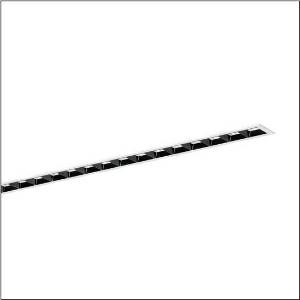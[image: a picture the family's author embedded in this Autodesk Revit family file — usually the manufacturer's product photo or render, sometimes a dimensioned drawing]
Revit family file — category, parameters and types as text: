
# Revit family: silica_r__21_51mx14dp4awb_d613
name_source: partatom
category: Lighting Fixtures
units: mm (PartAtom-declared; Revit-internal decimal feet)

## family parameters
Cut with Voids When Loaded = No
Host = Face
Light Source = No
Part Type = Normal
Room Calculation Point = No
Round Connector Dimension = Use Diameter
Shared = No

## types (1)
- --- (1 x LED, 11880 lm, 80.7 W, 4000K)
    Apparent Load = 81 VA
    CIE Flux Codes = 74 94 99 100 100
    Color Rendering = 80
    Color Temperature = 4000K
    Default Elevation = 1800 mm
    Description = Silica® 21, office luminaire, primary light control with darklight reflector, of PMMA, black, light emission: direct distribution, primary light characteristic: asymmetric, installation type: recessed, LED, rated luminous flux: 11.880lm, luminous efficacy: 147lm/W, light colour: 840, colour temperature: 4000K, control gear: DALI 2, with terminal, 3+2-pole, max. 2.5mm², mains connection: 220..240V, AC, 50/60Hz, rated input power: 80.7W, luminaire housing, of aluminium, traffic white (RAL 9016), length: 3.300mm, width: 79mm, height: 53mm, protection rating (complete): IP20, insulation class (complete): insulation class I (protective earthing), certification: CE, ENEC, VDE, permissible operating ambient temperature: 0..+35°C, standard: EN 50419, packaging unit: 1 piece
    Height = 0 mm  [stored 0 ft]
    Lamp = 1 x LED
    Lamp Light Flux = 11880 lm
    Lamp Power = 80.7 W
    Lamp count = 1
    Length = 3327 mm
    Luminous efficacy = 147 lm/W
    Manufacturer = Siteco
    ModVariant = No
    Model = 51MX14DP4AWB
    Mounting Place = Ceiling
    Mounting Type = Recessed
    Number of Poles = 1
    OnlyDefault = Yes
    Power Factor = 1
    Product Name = Silica® 21
    Product group = office luminaire | ceiling recessed
    ProductGroupID = 400
    Protection Class = Protection class I
    Protection Degree = IP 20
    RLX_Detail_Level = 1
    RLX_Emergency_Light_Flux = 0 lm
    RLX_Emergency_Type = 0
    RLX_Emergency_Type_DB = No
    RlxData = <blob elided: 33281 chars, md5=3f512f17>
    Socket = socket
    Standby Power = 0 W
    System Light Flux = 11880 lm
    System Power = 81 W
    Type Comments = factory setting: luminous flux: 100 % | dim-lin: 254 | 418 mA
    Type Image = l_1335880.jpg
    URL = http://relux.com
    VarID = @adj_062383
    Voltage = 0 V
    Weight = 0.00 kg
    Width = 79 mm

note: [stored X ft] marks values corroborated as IEEE doubles in the binary element streams (Revit-internal decimal feet)

## geometry (parser evidence)
native form markers: Blend x4, Sweep x11
no freeform markers — native parametric forms only
